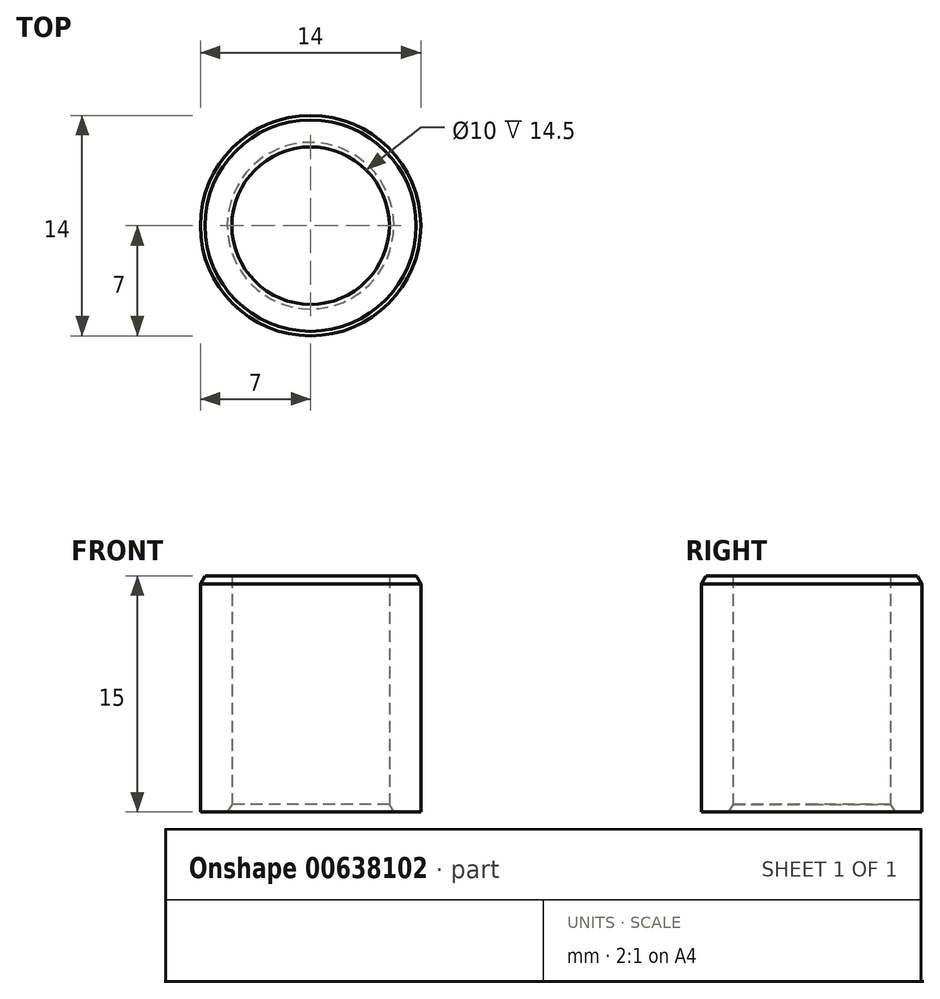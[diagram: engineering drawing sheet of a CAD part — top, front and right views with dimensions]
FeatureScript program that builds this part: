
annotation { "Feature Type Name" : "Feature", "Feature Type Description" : "" }
export const myFeature = defineFeature(function(context is Context, id is Id, definition is map)
    precondition{}
    {
        {
            var Q0;
            Q0=qCreatedBy(makeId("Top.planeOp"),FACE);
            var sketch = newSketch(context, id + "F0", { "sketchPlane" : qUnion([Q0])});
            skCircle(sketch, "E0", {"center": v(0, 0) * mm, "radius": 5 * mm});
            skCircle(sketch, "E1", {"center": v(0, 0) * mm, "radius": 7 * mm});
            skSolve(sketch);
        }
        {
            var Q0;
            Q0 = qSketchRegion(id + "F0", true);
            extrude(context, id + "F1", {"entities" : qUnion([Q0]), "depth" : 15 * mm, "offsetDistance" : 25 * mm});
        }
        {
            var Q0;
            Q0=makeQuery(id+"F1.opExtrude","CAP_EDGE",EDGE,{"disambiguationData":[OSD([sQuery(id+"F0.wireOp",EDGE,"E1")])],"isStart":false});
            chamfer(context, id + "F2", {"entities" : qUnion([Q0]), "chamferType" : ChamferType.OFFSET_ANGLE, "width" : 0.5 * mm, "oppositeDirection" : true, "angle" : 30 * degree, "tangentPropagation" : true});
        }
        {
            var Q0;
            Q0=makeQuery(id+"F1.opExtrude","CAP_EDGE",EDGE,{"disambiguationData":[OSD([sQuery(id+"F0.wireOp",EDGE,"E0")])],"isStart":true});
            chamfer(context, id + "F3", {"entities" : qUnion([Q0]), "chamferType" : ChamferType.OFFSET_ANGLE, "width" : 0.5 * mm, "oppositeDirection" : true, "angle" : 30 * degree, "tangentPropagation" : true});
        }
    });
